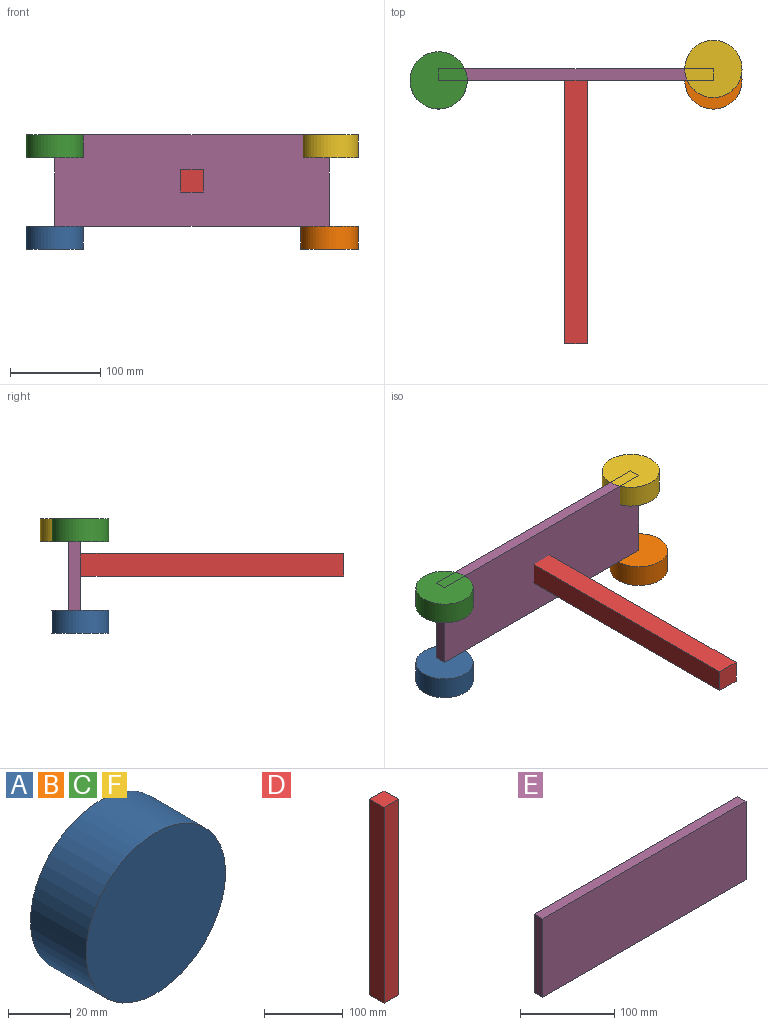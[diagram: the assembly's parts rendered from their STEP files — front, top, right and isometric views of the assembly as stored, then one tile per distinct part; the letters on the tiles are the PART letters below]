
ASSEMBLY  parts=6 mates=5
PART A: 3 faces, bbox 63.5x25.4x63.5 mm
  f0: cylinder r=31.75mm len=63.5mm, axis (0,1,0), area 5067.1mm2, adj f1,f2
  f1: plane 63.5x63.5mm, normal (0,-1,0), area 3166.9mm2, adj f0
  f2: plane 63.5x63.5mm, normal (0,1,0), area 3166.9mm2, adj f0
PART B: same geometry as A
PART C: same geometry as A
PART D: 6 faces, bbox 25.4x25.4x304.8 mm
  f0: plane 25.4x25.4mm, normal (0,0,1), area 645.2mm2, adj f1,f3,f4,f5
  f1: plane 304.8x25.4mm, normal (-1,0,0), area 7741.9mm2, adj f0,f2,f4,f5
  f2: plane 25.4x25.4mm, normal (0,0,-1), area 645.2mm2, adj f1,f3,f4,f5
  f3: plane 304.8x25.4mm, normal (1,0,0), area 7741.9mm2, adj f0,f2,f4,f5
  f4: plane 304.8x25.4mm, normal (0,-1,0), area 7741.9mm2, adj f0,f1,f2,f3
  f5: plane 304.8x25.4mm, normal (0,1,0), area 7741.9mm2, adj f0,f1,f2,f3
PART E: 6 faces, bbox 304.8x12.7x101.6 mm
  f0: plane 304.8x12.7mm, normal (0,0,1), area 3871mm2, adj f1,f3,f4,f5
  f1: plane 101.6x12.7mm, normal (-1,0,0), area 1290.3mm2, adj f0,f2,f4,f5
  f2: plane 304.8x12.7mm, normal (0,0,-1), area 3871mm2, adj f1,f3,f4,f5
  f3: plane 101.6x12.7mm, normal (1,0,0), area 1290.3mm2, adj f0,f2,f4,f5
  f4: plane 304.8x101.6mm, normal (0,-1,0), area 30967.7mm2, adj f0,f1,f2,f3
  f5: plane 304.8x101.6mm, normal (0,1,0), area 30967.7mm2, adj f0,f1,f2,f3
PART F: same geometry as A
PLACE A rot(axis=(-1,0,0),90deg) t=(-142.86,-12.7,-192.66)mm
PLACE B rot(axis=(-1,0,0),90deg) t=(161.94,-12.7,-192.66)mm
PLACE C rot(axis=(-1,0,0),90deg) t=(-142.86,-12.7,-91.06)mm
PLACE D rot(axis=(1,0,0),90deg) t=(50.61,-164.36,-103.76)mm
PLACE E at identity
PLACE F rot(axis=(1,0,0),90deg) t=(161.94,0,-65.66)mm
MATE fastened A.f0 <-> E.f2  axis (0,0,1) through (-142.86,-12.7,-167.26)mm
MATE fastened C.f0 <-> E.f0  axis (0,0,1) through (-142.86,-12.7,-65.66)mm
MATE fastened B.f0 <-> E.f2  axis (0,0,1) through (161.94,-12.7,-167.26)mm
MATE fastened F.f0 <-> E.f0  axis (0,0,1) through (161.94,0,-65.66)mm
MATE fastened D.f2 <-> E.f5  axis (0,1,0) through (9.54,0,-116.46)mm
